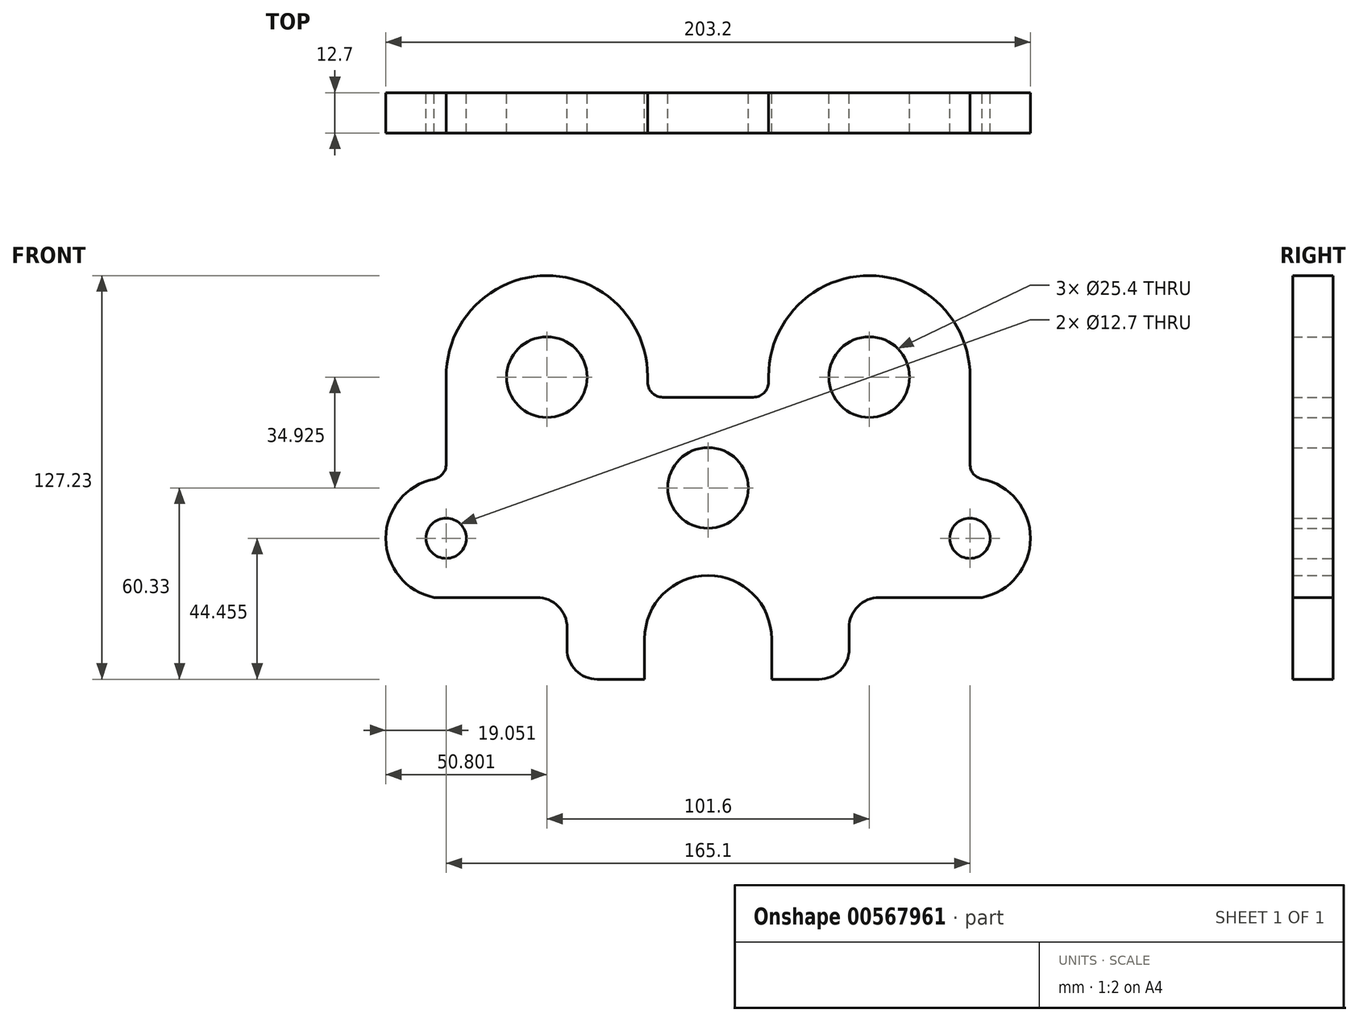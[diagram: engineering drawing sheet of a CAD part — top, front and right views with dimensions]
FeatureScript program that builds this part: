
annotation { "Feature Type Name" : "Feature", "Feature Type Description" : "" }
export const myFeature = defineFeature(function(context is Context, id is Id, definition is map)
    precondition{}
    {
        {
            var Q0;
            Q0=qCreatedBy(makeId("Front.planeOp"),FACE);
            var sketch = newSketch(context, id + "F0", { "sketchPlane" : qUnion([Q0])});
            skLineSegment(sketch, "E0", {"start": v(-9.63, 88.85) * mm, "end": v(-9.63, -64.64) * mm, "construction": true});
            skLineSegment(sketch, "E1", {"start": v(-95.99, 9.75) * mm, "end": v(85.8, 9.75) * mm, "construction": true});
            skLineSegment(sketch, "E2", {"start": v(41.17, 57.01) * mm, "end": v(41.17, 34.15) * mm, "construction": true});
            skLineSegment(sketch, "E3", {"start": v(72.92, 5.5) * mm, "end": v(72.92, -21.18) * mm, "construction": true});
            skLineSegment(sketch, "E4", {"start": v(-35.03, -37.88) * mm, "end": v(12.5, -37.88) * mm, "construction": true});
            skLineSegment(sketch, "E5", {"start": v(53.64, -6.13) * mm, "end": v(93.08, -6.13) * mm, "construction": true});
            skLineSegment(sketch, "E6", {"start": v(22.15, 44.67) * mm, "end": v(61.59, 44.67) * mm, "construction": true});
            skPoint(sketch, "E7", {"position": v(41.17, 44.67) * mm});
            skPoint(sketch, "E8", {"position": v(72.92, -6.13) * mm});
            skPoint(sketch, "E9", {"position": v(-9.63, -37.88) * mm});
            skCircle(sketch, "E10", {"center": v(41.17, 44.67) * mm, "radius": 12.7 * mm});
            skCircle(sketch, "E11", {"center": v(72.92, -6.13) * mm, "radius": 6.35 * mm});
            skCircle(sketch, "E12", {"center": v(-9.63, 9.75) * mm, "radius": 12.7 * mm});
            skLineSegment(sketch, "E13", {"start": v(-23.92, 38.32) * mm, "end": v(4.66, 38.32) * mm});
            skLineSegment(sketch, "E14", {"start": v(9.42, 44.9) * mm, "end": v(9.42, 43.09) * mm});
            skLineSegment(sketch, "E15", {"start": v(72.92, 44.67) * mm, "end": v(72.92, 17.2) * mm});
            skLineSegment(sketch, "E16", {"start": v(10.39, -50.58) * mm, "end": v(25.3, -50.58) * mm});
            skLineSegment(sketch, "E17", {"start": v(34.82, -41.05) * mm, "end": v(34.82, -34.32) * mm});
            skLineSegment(sketch, "E18", {"start": v(44.35, -24.8) * mm, "end": v(72.92, -24.8) * mm});
            skLineSegment(sketch, "E19", {"start": v(72.92, -24.8) * mm, "end": v(76.73, -24.8) * mm});
            skArc(sketch, "E20", {"start": v(9.42, 44.9) * mm, "mid": v(41.28, 76.65) * mm, "end": v(72.92, 44.67) * mm});
            skPoint(sketch, "E21.visualSharp", {"position": v(34.82, -24.8) * mm});
            skArc(sketch, "E21.filletArc", {"start": v(44.35, -24.8) * mm, "mid": v(37.61, -27.58) * mm, "end": v(34.82, -34.32) * mm});
            skPoint(sketch, "E22.visualSharp", {"position": v(34.82, -50.58) * mm});
            skArc(sketch, "E22.filletArc", {"start": v(25.3, -50.58) * mm, "mid": v(32.03, -47.79) * mm, "end": v(34.82, -41.05) * mm});
            skPoint(sketch, "E23.visualSharp", {"position": v(72.92, 12.92) * mm});
            skArc(sketch, "E23.filletArc", {"start": v(72.92, 17.2) * mm, "mid": v(74, 14.2) * mm, "end": v(76.73, 12.54) * mm});
            skArc(sketch, "E24", {"start": v(76.73, 12.54) * mm, "mid": v(91.97, -6.13) * mm, "end": v(76.73, -24.8) * mm});
            skLineSegment(sketch, "E25", {"start": v(10.39, -50.58) * mm, "end": v(10.39, -37.88) * mm});
            skLineSegment(sketch, "E26.MirrorCS", {"start": v(-29.65, -50.58) * mm, "end": v(-29.65, -37.88) * mm});
            skLineSegment(sketch, "E27.MirrorCS", {"start": v(-29.65, -50.58) * mm, "end": v(-44.55, -50.58) * mm});
            skArc(sketch, "E28.MirrorCS", {"start": v(-44.55, -50.58) * mm, "mid": v(-51.29, -47.79) * mm, "end": v(-54.08, -41.05) * mm});
            skLineSegment(sketch, "E29.MirrorCS", {"start": v(-54.08, -41.05) * mm, "end": v(-54.08, -34.32) * mm});
            skArc(sketch, "E30.MirrorCS", {"start": v(-63.6, -24.8) * mm, "mid": v(-56.87, -27.58) * mm, "end": v(-54.08, -34.32) * mm});
            skLineSegment(sketch, "E31.MirrorCS", {"start": v(-63.6, -24.8) * mm, "end": v(-92.18, -24.8) * mm});
            skLineSegment(sketch, "E32.MirrorCS", {"start": v(-92.18, -24.8) * mm, "end": v(-95.99, -24.8) * mm});
            skArc(sketch, "E33.MirrorCS", {"start": v(-95.99, 12.54) * mm, "mid": v(-111.23, -6.13) * mm, "end": v(-95.99, -24.8) * mm});
            skArc(sketch, "E34.MirrorCS", {"start": v(-92.18, 17.2) * mm, "mid": v(-93.25, 14.2) * mm, "end": v(-95.99, 12.54) * mm});
            skLineSegment(sketch, "E35.MirrorCS", {"start": v(-92.18, 44.67) * mm, "end": v(-92.18, 17.2) * mm});
            skArc(sketch, "E36.MirrorCS", {"start": v(-28.68, 44.9) * mm, "mid": v(-60.54, 76.65) * mm, "end": v(-92.18, 44.67) * mm});
            skLineSegment(sketch, "E37.MirrorCS", {"start": v(-28.68, 44.9) * mm, "end": v(-28.68, 43.09) * mm});
            skArc(sketch, "E38", {"start": v(-29.65, -37.88) * mm, "mid": v(-9.63, -17.86) * mm, "end": v(10.39, -37.88) * mm});
            skCircle(sketch, "E39.MirrorC", {"center": v(-60.43, 44.67) * mm, "radius": 12.7 * mm});
            skCircle(sketch, "E40.MirrorC", {"center": v(-92.18, -6.13) * mm, "radius": 6.35 * mm});
            skPoint(sketch, "E41.visualSharp", {"position": v(-28.68, 38.32) * mm});
            skArc(sketch, "E41.filletArc", {"start": v(-28.68, 43.09) * mm, "mid": v(-27.28, 39.72) * mm, "end": v(-23.92, 38.32) * mm});
            skPoint(sketch, "E42.visualSharp", {"position": v(9.42, 38.32) * mm});
            skArc(sketch, "E42.filletArc", {"start": v(4.66, 38.32) * mm, "mid": v(8.03, 39.72) * mm, "end": v(9.42, 43.09) * mm});
            skSolve(sketch);
        }
        {
            var Q0;
            Q0 = qSketchRegion(id + "F0", true);
            extrude(context, id + "F1", {"entities" : qUnion([Q0]), "depth" : 12.7 * mm, "offsetDistance" : 25.4 * mm});
        }
    });
